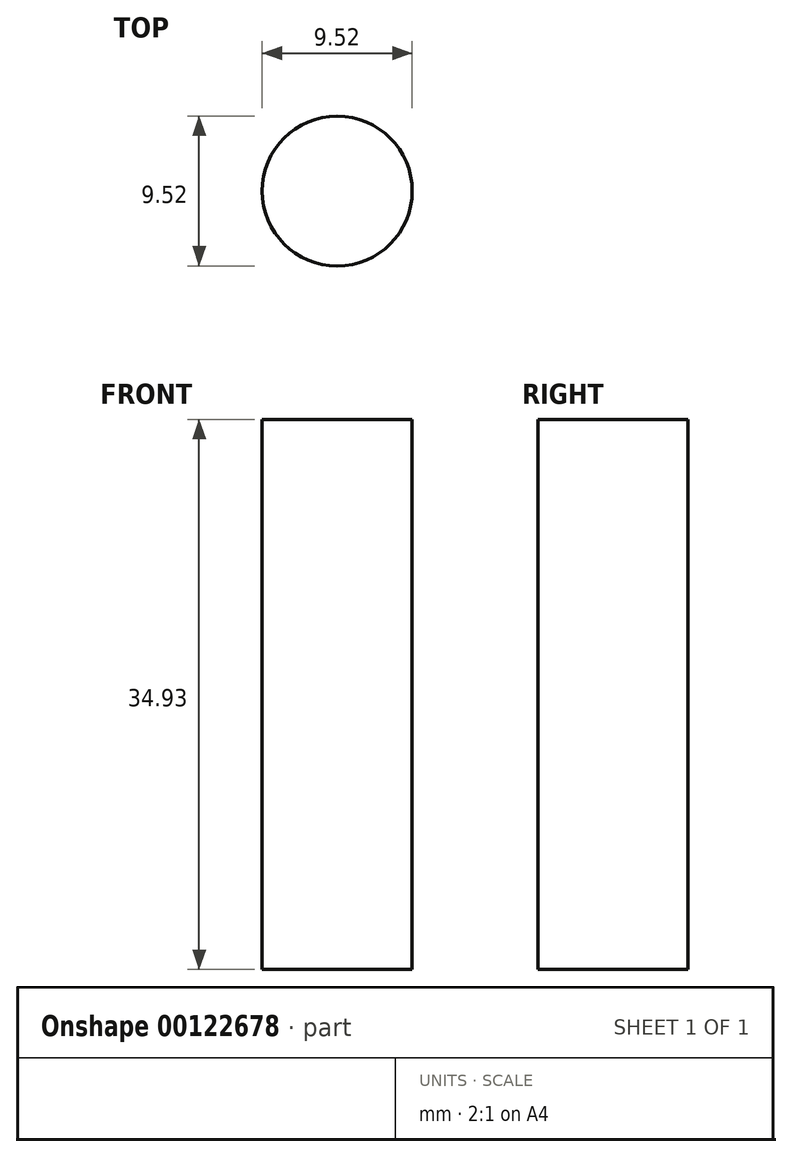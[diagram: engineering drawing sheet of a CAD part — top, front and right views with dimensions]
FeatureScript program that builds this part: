
annotation { "Feature Type Name" : "Feature", "Feature Type Description" : "" }
export const myFeature = defineFeature(function(context is Context, id is Id, definition is map)
    precondition{}
    {
        {
            var Q0;
            Q0=qCreatedBy(makeId("Top.planeOp"),FACE);
            var sketch = newSketch(context, id + "F0", { "sketchPlane" : qUnion([Q0])});
            skCircle(sketch, "E0", {"center": v(0, 0) * mm, "radius": 4.76 * mm});
            skSolve(sketch);
        }
        {
            var Q0;
            Q0=makeQuery(id+"F0.imprint","IMPRINT",FACE,{"disambiguationData":[TD([[makeQuery(id+"F0.imprint","IMPRINT",EDGE,{"derivedFrom":sQuery(id+"F0.wireOp",EDGE,"E0")}),1.0]])]});
            extrude(context, id + "F1", {"entities" : qUnion([Q0]), "depth" : 34.92 * mm});
        }
    });
